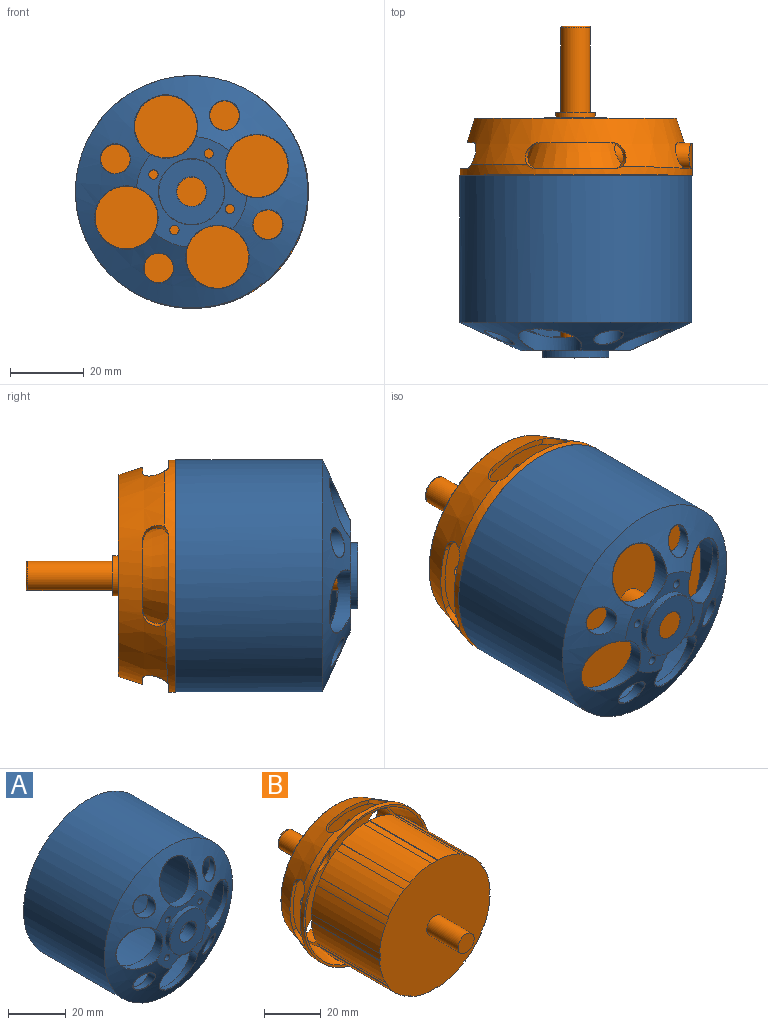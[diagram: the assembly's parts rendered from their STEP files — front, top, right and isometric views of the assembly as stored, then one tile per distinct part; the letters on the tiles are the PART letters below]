
ASSEMBLY  parts=2 mates=1
PART A: 38 faces, bbox 63x49.4x63 mm
  f0: plane 63x63mm, normal (0,1,0), area 141.2mm2, adj f7,f27
  f1: plane 61.56x61.56mm, normal (0,1,0), area 491.3mm2, adj f27,f28
  f2: torus R=8.9mm, axis (0,-1,0), area 8.8mm2, adj f3,f4
  f3: plane 17.8x17.8mm, normal (0,-1,0), area 196mm2, adj f2,f5
  f4: cylinder r=9mm len=18mm, axis (0,-1,0), area 107.4mm2, adj f2,f13
  f5: torus R=4.1mm, axis (0,1,0), area 4mm2, adj f3,f6
  f6: cylinder r=4mm len=8mm, axis (0,1,0), area 123.2mm2, adj f5,f9
  f7: cylinder r=31.5mm len=63mm, axis (0,1,0), area 7866mm2, adj f0,f23
  f8: cylinder r=1.26mm len=3.86mm, axis (0,1,0), area 28.6mm2, adj f13,f14
  f9: plane 18x18mm, normal (0,1,0), area 204.2mm2, adj f6,f14
  f10: torus R=8.6mm, axis (0,1,0), area 2.3mm2, adj f11,f12,f13,f23
  f11: bspline ~17.23x14.16mm, area 7.5mm2, adj f10,f12,f23
  f12: cylinder r=8.5mm len=17mm, axis (0,1,0), area 156.5mm2, adj f10,f11,f14
  f13: plane 26.98x26.98mm, normal (0,-1,0), area 265.5mm2, adj f4,f8,f10,f15,f18,f23,f24,f35
  f14: cone r=18.56mm half-angle=75.3deg, axis (0,1,0), area 1141.1mm2, adj f8,f9,f12,f17,f20,f22,f26,f28
  f15: torus R=8.6mm, axis (0,1,0), area 2.3mm2, adj f13,f16,f17,f23
  f16: bspline ~17.23x14.16mm, area 7.5mm2, adj f15,f17,f23
  f17: cylinder r=8.5mm len=17mm, axis (0,1,0), area 164.4mm2, adj f14,f15,f16
  f18: torus R=8.6mm, axis (0,1,0), area 2.3mm2, adj f13,f19,f20,f23
  f19: bspline ~18.32x14.34mm, area 7.4mm2, adj f18,f20,f23
  f20: cylinder r=8.5mm len=17mm, axis (0,1,0), area 156.5mm2, adj f14,f18,f19
  f21: bspline ~8.66x8.33mm, area 4.3mm2, adj f22,f23
  f22: cylinder r=4mm len=8mm, axis (0,1,0), area 73.2mm2, adj f14,f21
  f23: cone r=23.65mm half-angle=65.2deg, axis (0,1,0), area 1578.1mm2, adj f7,f10,f11,f13,f15,f16,f18,f19
  f24: torus R=8.6mm, axis (0,1,0), area 2.3mm2, adj f13,f23,f25,f26
  f25: bspline ~17.23x14.16mm, area 7.4mm2, adj f23,f24,f26
  f26: cylinder r=8.5mm len=17mm, axis (0,1,0), area 164.3mm2, adj f14,f24,f25
  f27: cylinder r=30.78mm len=61.56mm, axis (0,1,0), area 3mm2, adj f0,f1
  f28: cylinder r=28.12mm len=56.25mm, axis (0,1,0), area 6955.3mm2, adj f1,f14
  f29: bspline ~8.66x8.33mm, area 4.3mm2, adj f23,f30
  f30: cylinder r=4mm len=8mm, axis (0,1,0), area 73.2mm2, adj f14,f29
  f31: bspline ~8.66x8.33mm, area 4.3mm2, adj f23,f32
  f32: cylinder r=4mm len=8mm, axis (0,1,0), area 73.2mm2, adj f14,f31
  f33: bspline ~8.2x8.2mm, area 4.3mm2, adj f23,f34
  f34: cylinder r=4mm len=8mm, axis (0,1,0), area 73.2mm2, adj f14,f33
  f35: cylinder r=1.26mm len=3.86mm, axis (0,1,0), area 28.6mm2, adj f13,f14
  f36: cylinder r=1.26mm len=3.86mm, axis (0,1,0), area 28.6mm2, adj f13,f14
  f37: cylinder r=1.26mm len=3.86mm, axis (0,1,0), area 28.6mm2, adj f13,f14
PART B: 125 faces, bbox 63.5x90x63.5 mm
  f0: torus R=1.77mm, axis (0,-1,0), area 1.7mm2, adj f1,f2
  f1: plane 54.21x54.21mm, normal (0,1,0), area 1480.9mm2, adj f0,f3,f5,f78,f79,f96,f98,f100
  f2: cylinder r=1.67mm len=6.08mm, axis (0,-1,0), area 63.6mm2, adj f0,f30
  f3: torus R=1.77mm, axis (0,-1,0), area 1.7mm2, adj f1,f4
  f4: cylinder r=1.67mm len=6.08mm, axis (0,-1,0), area 63.6mm2, adj f3,f30
  f5: torus R=6.1mm, axis (0,1,0), area 6mm2, adj f1,f6
  f6: cylinder r=6mm len=12mm, axis (0,-1,0), area 229.1mm2, adj f5,f30
  f7: plane 10.76x10.76mm, normal (0,1,0), area 40.7mm2, adj f80,f92
  f8: cylinder r=27.27mm len=33.98mm, axis (0,-1,0), area 105.6mm2, adj f53,f54,f66,f67
  f9: cylinder r=27.27mm len=33.98mm, axis (0,-1,0), area 105.6mm2, adj f51,f52,f66,f67
  f10: cylinder r=27.27mm len=33.98mm, axis (0,-1,0), area 105.6mm2, adj f49,f50,f66,f67
  f11: cylinder r=27.27mm len=33.98mm, axis (0,-1,0), area 105.6mm2, adj f47,f48,f66,f67
  f12: cylinder r=27.27mm len=33.98mm, axis (0,-1,0), area 105.6mm2, adj f45,f46,f66,f67
  f13: cylinder r=27.27mm len=33.98mm, axis (0,-1,0), area 105.6mm2, adj f43,f44,f66,f67
  f14: cylinder r=27.27mm len=33.98mm, axis (0,-1,0), area 105.6mm2, adj f41,f42,f66,f67
  f15: cylinder r=27.27mm len=33.98mm, axis (0,-1,0), area 105.6mm2, adj f39,f40,f66,f67
  f16: cylinder r=27.27mm len=33.98mm, axis (0,-1,0), area 105.6mm2, adj f37,f38,f66,f67
  f17: cylinder r=27.27mm len=33.98mm, axis (0,-1,0), area 105.6mm2, adj f35,f36,f66,f67
  f18: cylinder r=27.27mm len=33.98mm, axis (0,-1,0), area 105.6mm2, adj f33,f34,f66,f67
  f19: cylinder r=27.27mm len=33.98mm, axis (0,-1,0), area 105.6mm2, adj f31,f32,f66,f67
  f20: plane 15.83x8.19mm, normal (0,-1,0), area 125.7mm2, adj f22,f70,f71,f82
  f21: plane 8.19x0.3mm, normal (0,-1,0), area 0.2mm2, adj f22,f82,f83,f90
  f22: cylinder r=3.47mm len=20.82mm, axis (-1,0,0), area 209.8mm2, adj f20,f21,f68,f70,f71,f81,f83,f90
  f23: plane 21.49x3.05mm, normal (0,1,0), area 27.4mm2, adj f71,f73,f74,f89
  f24: plane 19.79x3.17mm, normal (0,-1,0), area 31.5mm2, adj f71,f73,f74,f83
  f25: plane 19.79x3.17mm, normal (0,-1,0), area 31.5mm2, adj f71,f83,f86,f88
  f26: plane 19.79x3.17mm, normal (0,-1,0), area 31.5mm2, adj f71,f75,f83,f85
  f27: plane 21.75x3.38mm, normal (0,1,0), area 34.3mm2, adj f71,f76,f77,f83,f89
  f28: plane 19.79x3.17mm, normal (0,-1,0), area 31.5mm2, adj f71,f76,f77,f83
  f29: plane 63x63mm, normal (0,-1,0), area 179.2mm2, adj f71,f89
  f30: plane 55.32x55.32mm, normal (0,-1,0), area 1437.5mm2, adj f2,f4,f6,f70,f71,f97,f99,f101
  f31: plane 33.98x0.29mm, normal (-1,0,0.06), area 10mm2, adj f19,f55,f66,f67
  f32: plane 33.98x0.29mm, normal (1,0,0.06), area 10mm2, adj f19,f65,f66,f67
  f33: plane 33.98x0.26mm, normal (-0.89,0,-0.45), area 10mm2, adj f18,f65,f66,f67
  f34: plane 33.98x0.25mm, normal (0.84,0,0.55), area 10mm2, adj f18,f64,f66,f67
  f35: plane 33.98x0.25mm, normal (-0.55,0,-0.84), area 10mm2, adj f17,f64,f66,f67
  f36: plane 33.98x0.26mm, normal (0.45,0,0.89), area 10mm2, adj f17,f63,f66,f67
  f37: plane 33.98x0.29mm, normal (-0.06,0,-1), area 10mm2, adj f16,f63,f66,f67
  f38: plane 33.98x0.29mm, normal (-0.06,0,1), area 10mm2, adj f16,f62,f66,f67
  f39: plane 33.98x0.26mm, normal (0.45,0,-0.89), area 10mm2, adj f15,f62,f66,f67
  f40: plane 33.98x0.25mm, normal (-0.55,0,0.84), area 10mm2, adj f15,f61,f66,f67
  f41: plane 33.98x0.25mm, normal (0.84,0,-0.55), area 10mm2, adj f14,f61,f66,f67
  f42: plane 33.98x0.26mm, normal (-0.89,0,0.45), area 10mm2, adj f14,f60,f66,f67
  f43: plane 33.98x0.29mm, normal (1,0,-0.06), area 10mm2, adj f13,f60,f66,f67
  f44: plane 33.98x0.29mm, normal (-1,0,-0.06), area 10mm2, adj f13,f59,f66,f67
  f45: plane 33.98x0.26mm, normal (0.89,0,0.45), area 10mm2, adj f12,f59,f66,f67
  f46: plane 33.98x0.25mm, normal (-0.84,0,-0.55), area 10mm2, adj f12,f58,f66,f67
  f47: plane 33.98x0.25mm, normal (0.55,0,0.84), area 10mm2, adj f11,f58,f66,f67
  f48: plane 33.98x0.26mm, normal (-0.45,0,-0.89), area 10mm2, adj f11,f57,f66,f67
  f49: plane 33.98x0.29mm, normal (0.06,0,1), area 10mm2, adj f10,f57,f66,f67
  f50: plane 33.98x0.29mm, normal (0.06,0,-1), area 10mm2, adj f10,f56,f66,f67
  f51: plane 33.98x0.26mm, normal (-0.45,0,0.89), area 10mm2, adj f9,f56,f66,f67
  f52: plane 33.98x0.25mm, normal (0.55,0,-0.84), area 10mm2, adj f9,f66,f67,f72
  f53: plane 33.98x0.25mm, normal (-0.84,0,0.55), area 10mm2, adj f8,f66,f67,f72
  f54: plane 33.98x0.26mm, normal (0.89,0,-0.45), area 10mm2, adj f8,f55,f66,f67
  f55: cylinder r=27.57mm len=33.98mm, axis (0,1,0), area 383.7mm2, adj f31,f54,f66,f67
  f56: cylinder r=27.57mm len=33.98mm, axis (0,1,0), area 383.7mm2, adj f50,f51,f66,f67
  f57: cylinder r=27.57mm len=33.98mm, axis (0,1,0), area 383.7mm2, adj f48,f49,f66,f67
  f58: cylinder r=27.57mm len=33.98mm, axis (0,1,0), area 383.7mm2, adj f46,f47,f66,f67
  f59: cylinder r=27.57mm len=33.98mm, axis (0,1,0), area 383.7mm2, adj f44,f45,f66,f67
  f60: cylinder r=27.57mm len=33.98mm, axis (0,1,0), area 383.7mm2, adj f42,f43,f66,f67
  f61: cylinder r=27.57mm len=33.98mm, axis (0,1,0), area 383.7mm2, adj f40,f41,f66,f67
  f62: cylinder r=27.57mm len=33.98mm, axis (0,1,0), area 383.7mm2, adj f38,f39,f66,f67
  f63: cylinder r=27.57mm len=33.98mm, axis (0,1,0), area 383.7mm2, adj f36,f37,f66,f67
  f64: cylinder r=27.57mm len=33.98mm, axis (0,1,0), area 383.7mm2, adj f34,f35,f66,f67
  f65: cylinder r=27.57mm len=33.98mm, axis (0,1,0), area 383.7mm2, adj f32,f33,f66,f67
  f66: plane 55.05x55.05mm, normal (0,-1,0), area 2326.3mm2, adj f8,f9,f10,f11,f12,f13,f14,f15
  f67: plane 55.05x55.05mm, normal (0,1,0), area 1627.2mm2, adj f8,f9,f10,f11,f12,f13,f14,f15
  f68: plane 6.61x3.1mm, normal (0,1,0), area 10.4mm2, adj f22,f71,f75,f83
  f69: plane 18.92x18.92mm, normal (0,1,0), area 190.1mm2, adj f78,f80
  f70: cone r=15.44mm half-angle=21deg, axis (0,-1,0), area 745.4mm2, adj f20,f22,f30,f67,f81,f82
  f71: cone r=30.58mm half-angle=17.5deg, axis (0,-1,0), area 1031.3mm2, adj f20,f22,f23,f24,f25,f26,f27,f28
  f72: cylinder r=27.57mm len=33.98mm, axis (0,1,0), area 383.7mm2, adj f52,f53,f66,f67
  f73: cylinder r=3.51mm len=7.03mm, axis (0.89,0,0.45), area 19.9mm2, adj f23,f24,f71,f83,f89
  f74: cylinder r=3.51mm len=7.03mm, axis (-0.89,0,0.45), area 19.7mm2, adj f23,f24,f71,f83,f89
  f75: cylinder r=3.51mm len=7.03mm, axis (0.89,0,-0.45), area 18mm2, adj f26,f68,f71,f83
  f76: cylinder r=3.51mm len=7.03mm, axis (-0.45,0,0.89), area 18mm2, adj f27,f28,f71,f83
  f77: cylinder r=3.51mm len=7.03mm, axis (-0.45,0,-0.89), area 19.7mm2, adj f27,f28,f71,f83,f89
  f78: cylinder r=9.46mm len=18.92mm, axis (0,1,0), area 0.9mm2, adj f1,f69
  f79: torus R=27.1mm, axis (0,1,0), area 67mm2, adj f1,f83
  f80: cylinder r=5.38mm len=10.76mm, axis (0,-1,0), area 52.2mm2, adj f7,f69
  f81: plane 20.29x8.19mm, normal (0,1,0), area 161.4mm2, adj f22,f70,f82,f90
  f82: cylinder r=3.47mm len=20.79mm, axis (-1,0,0), area 209.2mm2, adj f20,f21,f70,f71,f81,f83,f84,f90
  f83: cone r=32.07mm half-angle=17.5deg, axis (0,-1,0), area 1786.9mm2, adj f21,f22,f24,f25,f26,f27,f28,f68
  f84: plane 6.6x3.1mm, normal (0,1,0), area 10.4mm2, adj f71,f82,f83,f85,f89
  f85: cylinder r=3.51mm len=7.03mm, axis (-0.89,0,-0.45), area 19.3mm2, adj f26,f71,f83,f84,f89
  f86: cylinder r=3.51mm len=7.03mm, axis (0.45,0,0.89), area 19.9mm2, adj f25,f71,f83,f87,f89
  f87: plane 21.53x3.1mm, normal (0,1,0), area 28.3mm2, adj f71,f86,f88,f89
  f88: cylinder r=3.51mm len=7.03mm, axis (0.45,0,-0.89), area 19.8mm2, adj f25,f71,f83,f87,f89
  f89: cylinder r=31.5mm len=63mm, axis (0,1,0), area 389.6mm2, adj f23,f27,f29,f73,f74,f77,f83,f84
  f90: cylinder r=31.5mm len=15.14mm, axis (0,1,0), area 95.2mm2, adj f21,f22,f81,f82
  f91: plane 7x7mm, normal (0,1,0), area 38.5mm2, adj f93
  f92: cylinder r=4mm len=22.96mm, axis (0,1,0), area 576.9mm2, adj f7,f93
  f93: torus R=3.5mm, axis (0,1,0), area 18.8mm2, adj f91,f92
  f94: plane 8x8mm, normal (0,-1,0), area 50.3mm2, adj f95
  f95: cylinder r=4mm len=15.59mm, axis (0,-1,0), area 391.9mm2, adj f66,f94
  f96: torus R=6.1mm, axis (0,1,0), area 6mm2, adj f1,f97
  f97: cylinder r=6mm len=12mm, axis (0,-1,0), area 229.1mm2, adj f30,f96
  f98: torus R=6.1mm, axis (0,1,0), area 6mm2, adj f1,f99
  f99: cylinder r=6mm len=12mm, axis (0,-1,0), area 229.1mm2, adj f30,f98
  f100: torus R=6.1mm, axis (0,1,0), area 6mm2, adj f1,f101
  f101: cylinder r=6mm len=12mm, axis (0,-1,0), area 229.1mm2, adj f30,f100
  f102: torus R=1.77mm, axis (0,-1,0), area 1.7mm2, adj f1,f103
  f103: cylinder r=1.67mm len=6.08mm, axis (0,-1,0), area 63.6mm2, adj f30,f102
  f104: torus R=1.77mm, axis (0,-1,0), area 1.7mm2, adj f1,f105
  f105: cylinder r=1.67mm len=6.08mm, axis (0,-1,0), area 63.6mm2, adj f30,f104
  f106: torus R=1.77mm, axis (0,-1,0), area 1.7mm2, adj f1,f107
  f107: cylinder r=1.67mm len=6.08mm, axis (0,-1,0), area 63.6mm2, adj f30,f106
  f108: torus R=1.77mm, axis (0,-1,0), area 1.7mm2, adj f1,f109
  f109: cylinder r=1.67mm len=6.08mm, axis (0,-1,0), area 63.6mm2, adj f30,f108
  f110: torus R=1.77mm, axis (0,-1,0), area 1.7mm2, adj f1,f111
  f111: cylinder r=1.67mm len=6.08mm, axis (0,-1,0), area 63.6mm2, adj f30,f110
  f112: torus R=1.77mm, axis (0,-1,0), area 1.7mm2, adj f1,f113
  f113: cylinder r=1.67mm len=6.08mm, axis (0,-1,0), area 63.6mm2, adj f30,f112
  f114: cylinder r=4mm len=8.66mm, axis (0,-1,0), area 130.4mm2, adj f115,f116,f117,f118,f121,f124
  f115: plane 6.95x2.66mm, normal (-1,0,0), area 11.1mm2, adj f114,f116,f117,f119,f120,f121
  f116: plane 8.19x4.43mm, normal (0,-1,0), area 5mm2, adj f114,f115,f117,f118,f119,f123
  f117: cone r=7.33mm half-angle=21deg, axis (0,1,0), area 203.1mm2, adj f114,f115,f116,f118,f119,f120,f121,f122
  f118: plane 6.95x2.66mm, normal (-1,0,0), area 11.1mm2, adj f114,f116,f117,f121,f122,f123
  f119: cylinder r=3.47mm len=1.7mm, axis (-1,0,0), area 0.3mm2, adj f115,f116,f117
  f120: cylinder r=3.47mm len=5.8mm, axis (-1,0,0), area 9.9mm2, adj f115,f117,f121
  f121: plane 8.19x7.1mm, normal (0,1,0), area 29.6mm2, adj f114,f115,f117,f118,f120,f122
  f122: cylinder r=3.47mm len=5.8mm, axis (-1,0,0), area 8.4mm2, adj f117,f118,f121
  f123: cylinder r=3.47mm len=1.7mm, axis (-1,0,0), area 0.3mm2, adj f116,f117,f118
  f124: plane 14.65x14.65mm, normal (0,-1,0), area 118.3mm2, adj f114,f117
PLACE A rot(axis=(0,-1,0),21.7deg) t=(7.01,22.81,32.98)mm
PLACE B t=(18.6,53.26,28.08)mm
MATE revolute B.f8 <-> A.f2  axis (0,-1,0) through (-0.01,-69.53,0.24)mm
